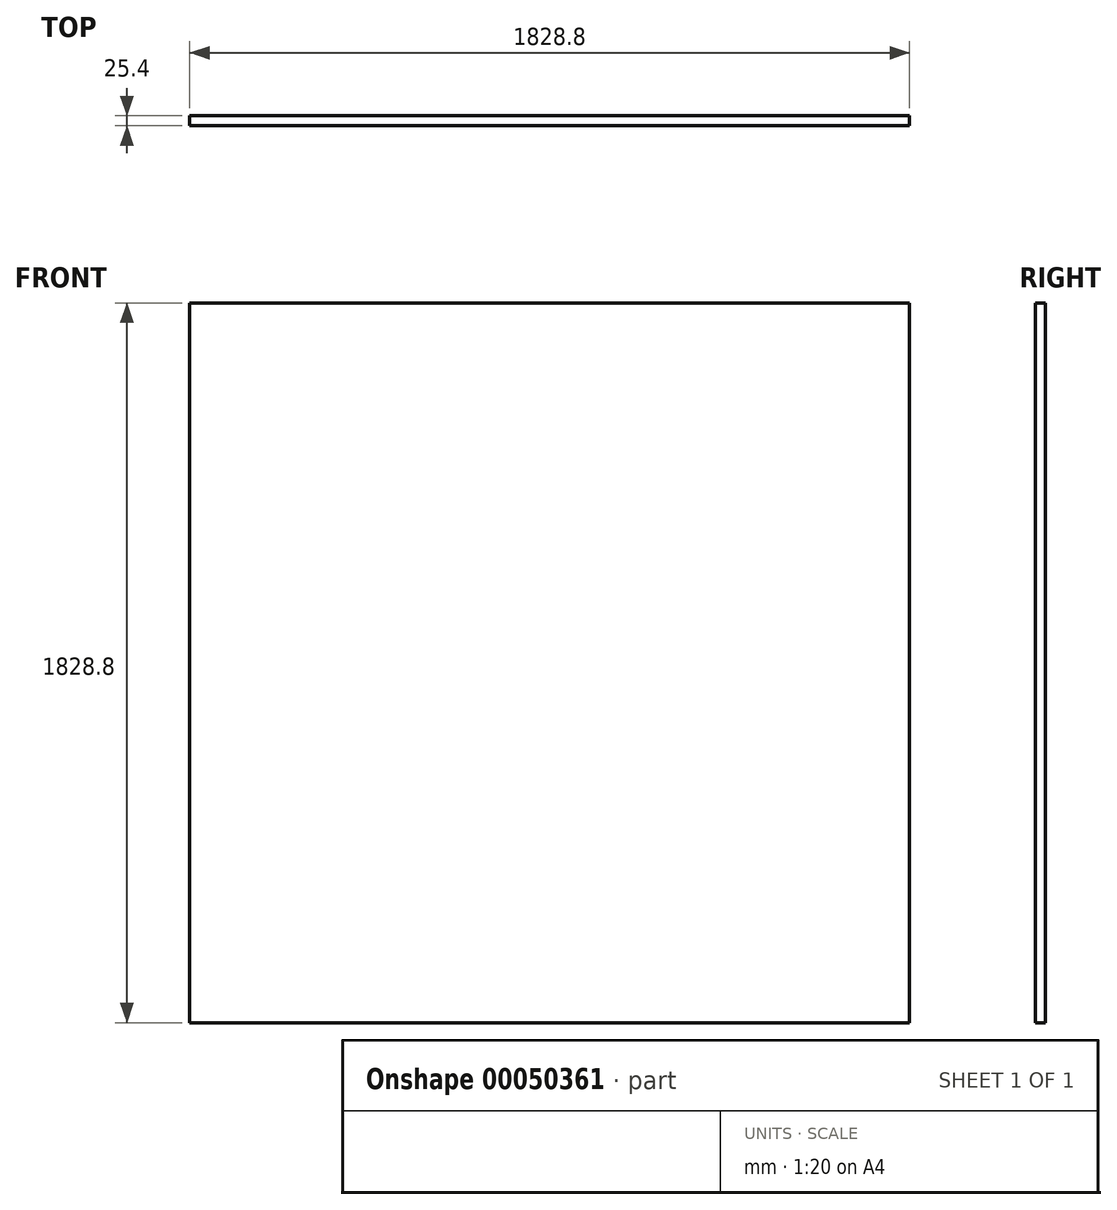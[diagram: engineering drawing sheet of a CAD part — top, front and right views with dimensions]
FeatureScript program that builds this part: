
annotation { "Feature Type Name" : "Feature", "Feature Type Description" : "" }
export const myFeature = defineFeature(function(context is Context, id is Id, definition is map)
    precondition{}
    {
        {
            var Q0;
            Q0=qCreatedBy(makeId("Front.planeOp"),FACE);
            var sketch = newSketch(context, id + "F0", { "sketchPlane" : qUnion([Q0])});
            skLineSegment(sketch, "E0.bottom", {"start": v(-916.99, 920.15) * mm, "end": v(911.81, 920.15) * mm});
            skLineSegment(sketch, "E0.top", {"start": v(-916.99, -908.65) * mm, "end": v(911.81, -908.65) * mm});
            skLineSegment(sketch, "E0.left", {"start": v(-916.99, 920.15) * mm, "end": v(-916.99, -908.65) * mm});
            skLineSegment(sketch, "E0.right", {"start": v(911.81, 920.15) * mm, "end": v(911.81, -908.65) * mm});
            skSolve(sketch);
        }
        {
            var Q0;
            Q0=makeQuery(id+"F0.imprint","IMPRINT",FACE,{"disambiguationData":[TD([[makeQuery(id+"F0.imprint","IMPRINT",EDGE,{"derivedFrom":sQuery(id+"F0.wireOp",EDGE,"E0.bottom")}),-1.0]])]});
            extrude(context, id + "F1", {"entities" : qUnion([Q0]), "depth" : 25.4 * mm});
        }
    });
